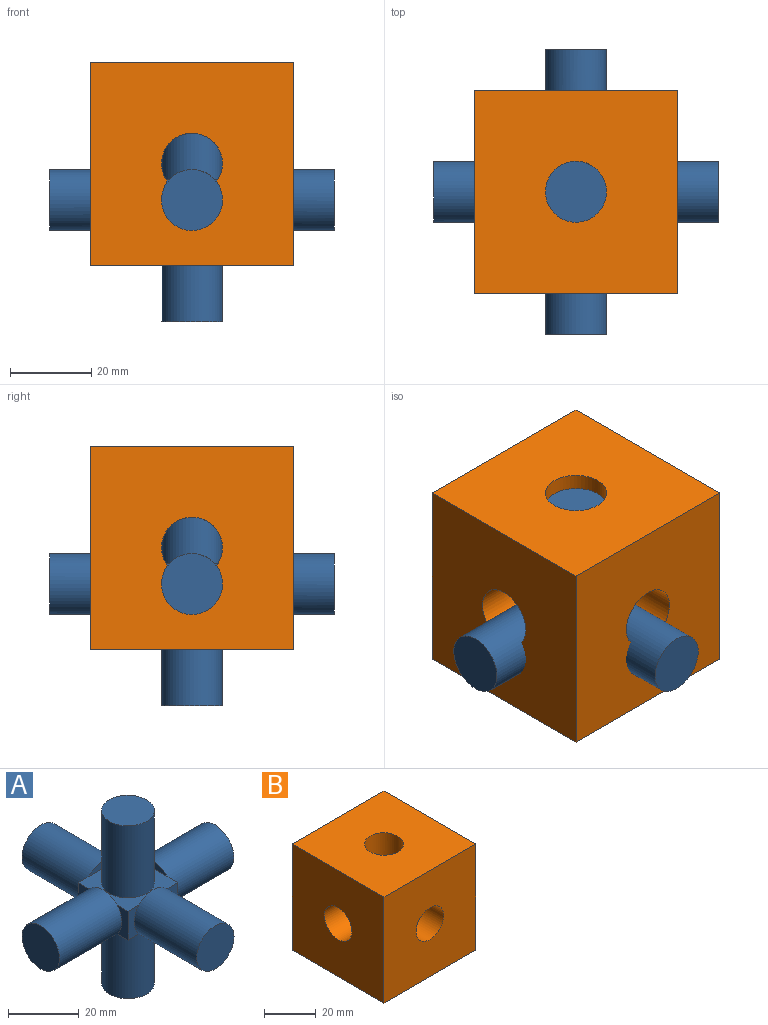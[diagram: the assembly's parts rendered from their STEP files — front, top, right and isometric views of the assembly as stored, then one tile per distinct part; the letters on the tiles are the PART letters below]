
ASSEMBLY  parts=2 mates=1
PART A: 30 faces, bbox 70x70x60 mm
  f0: plane 10x4.41mm, normal (0,1,0), area 31mm2, adj f5,f8,f9,f25
  f1: plane 10x4.41mm, normal (-1,0,0), area 31mm2, adj f6,f8,f9,f21
  f2: plane 10x4.41mm, normal (0,-1,0), area 31mm2, adj f7,f8,f9,f17
  f3: plane 10x4.41mm, normal (1,0,0), area 31mm2, adj f4,f8,f9,f13
  f4: plane 10x4.41mm, normal (0,-1,0), area 31mm2, adj f3,f8,f9,f17
  f5: plane 10x4.41mm, normal (1,0,0), area 31mm2, adj f0,f8,f9,f13
  f6: plane 10x4.41mm, normal (0,1,0), area 31mm2, adj f1,f8,f9,f25
  f7: plane 10x4.41mm, normal (-1,0,0), area 31mm2, adj f2,f8,f9,f21
  f8: plane 20x20mm, normal (0,0,1), area 223.3mm2, adj f0,f1,f2,f3,f4,f5,f6,f7
  f9: plane 20x20mm, normal (0,0,-1), area 223.3mm2, adj f0,f1,f2,f3,f4,f5,f6,f7
  f10: cylinder r=7.5mm len=25mm, axis (0,0,-1), area 1178.1mm2, adj f8,f11
  f11: plane 15x15mm, normal (0,0,1), area 176.7mm2, adj f10
  f12: plane 11.18x2.5mm, normal (-1,0,0), area 19.4mm2, adj f8,f13
  f13: cylinder r=7.5mm len=25mm, axis (-1,0,0), area 1178.1mm2, adj f3,f5,f12,f14,f15
  f14: plane 15x15mm, normal (1,0,0), area 176.7mm2, adj f13
  f15: plane 11.18x2.5mm, normal (-1,0,0), area 19.4mm2, adj f9,f13
  f16: plane 11.18x2.5mm, normal (0,1,0), area 19.4mm2, adj f8,f17
  f17: cylinder r=7.5mm len=25mm, axis (0,1,0), area 1178.1mm2, adj f2,f4,f16,f18,f19
  f18: plane 15x15mm, normal (0,-1,0), area 176.7mm2, adj f17
  f19: plane 11.18x2.5mm, normal (0,1,0), area 19.4mm2, adj f9,f17
  f20: plane 11.18x2.5mm, normal (1,0,0), area 19.4mm2, adj f9,f21
  f21: cylinder r=7.5mm len=25mm, axis (1,0,0), area 1178.1mm2, adj f1,f7,f20,f22,f23
  f22: plane 15x15mm, normal (-1,0,0), area 176.7mm2, adj f21
  f23: plane 11.18x2.5mm, normal (1,0,0), area 19.4mm2, adj f8,f21
  f24: plane 11.18x2.5mm, normal (0,-1,0), area 19.4mm2, adj f9,f25
  f25: cylinder r=7.5mm len=25mm, axis (0,-1,0), area 1178.1mm2, adj f0,f6,f24,f26,f27
  f26: plane 15x15mm, normal (0,1,0), area 176.7mm2, adj f25
  f27: plane 11.18x2.5mm, normal (0,-1,0), area 19.4mm2, adj f8,f25
  f28: cylinder r=7.5mm len=25mm, axis (0,0,1), area 1178.1mm2, adj f9,f29
  f29: plane 15x15mm, normal (0,0,-1), area 176.7mm2, adj f28
PART B: 12 faces, bbox 50x50x50 mm
  f0: cylinder r=7.5mm len=19.7mm, axis (1,0,0), area 859.9mm2, adj f2,f3,f7,f10,f11
  f1: cylinder r=7.5mm len=19.7mm, axis (1,0,0), area 859.9mm2, adj f2,f3,f5,f10,f11
  f2: cylinder r=7.5mm len=19.7mm, axis (0,-1,0), area 859.9mm2, adj f0,f1,f4,f10,f11
  f3: cylinder r=7.5mm len=19.7mm, axis (0,1,0), area 859.9mm2, adj f0,f1,f6,f10,f11
  f4: plane 50x50mm, normal (0,-1,0), area 2323.3mm2, adj f2,f5,f7,f8,f9
  f5: plane 50x50mm, normal (1,0,0), area 2323.3mm2, adj f1,f4,f6,f8,f9
  f6: plane 50x50mm, normal (0,1,0), area 2323.3mm2, adj f3,f5,f7,f8,f9
  f7: plane 50x50mm, normal (-1,0,0), area 2323.3mm2, adj f0,f4,f6,f8,f9
  f8: plane 50x50mm, normal (0,0,1), area 2323.3mm2, adj f4,f5,f6,f7,f10
  f9: plane 50x50mm, normal (0,0,-1), area 2323.3mm2, adj f4,f5,f6,f7,f11
  f10: cylinder r=7.5mm len=19.7mm, axis (0,0,1), area 859.9mm2, adj f0,f1,f2,f3,f8
  f11: cylinder r=7.5mm len=19.7mm, axis (0,0,-1), area 859.9mm2, adj f0,f1,f2,f3,f9
PLACE A t=(-21.65,-9.84,-9.95)mm
PLACE B t=(-21.65,-9.84,-21.01)mm fixed
MATE slider B.f10 <-> A.f10  axis (0,0,1) through (-21.65,-9.84,28.99)mm
